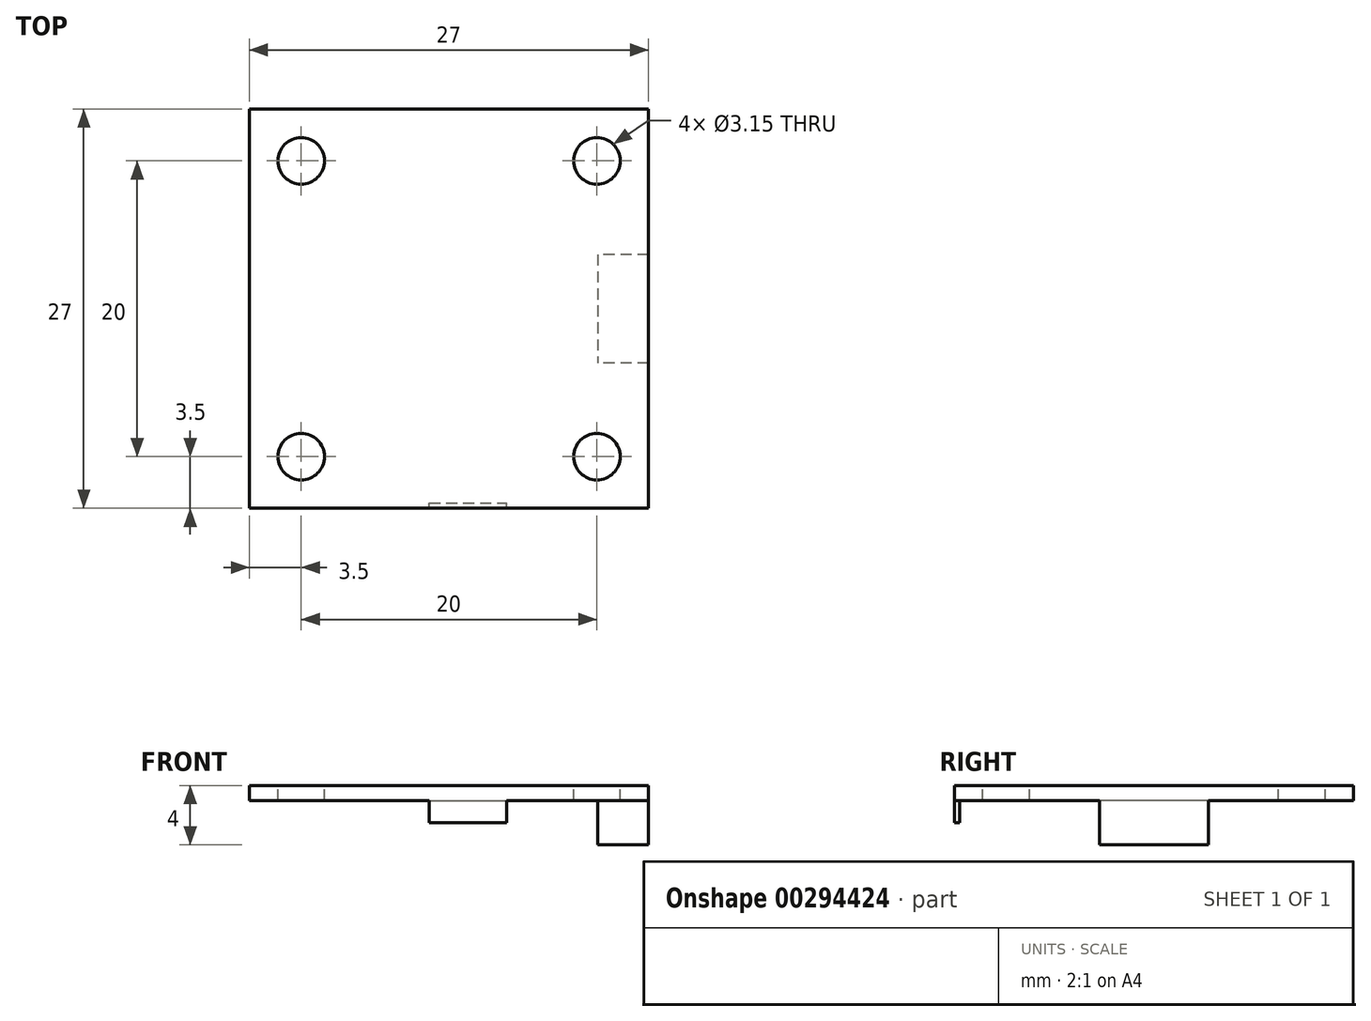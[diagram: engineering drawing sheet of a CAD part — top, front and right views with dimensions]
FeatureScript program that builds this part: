
annotation { "Feature Type Name" : "Feature", "Feature Type Description" : "" }
export const myFeature = defineFeature(function(context is Context, id is Id, definition is map)
    precondition{}
    {
        {
            var Q0;
            Q0=qCreatedBy(makeId("Top.planeOp"),FACE);
            var sketch = newSketch(context, id + "F0", { "sketchPlane" : qUnion([Q0])});
            skLineSegment(sketch, "E0.bottom", {"start": v(-13.5, 13.5) * mm, "end": v(13.5, 13.5) * mm});
            skLineSegment(sketch, "E0.top", {"start": v(-13.5, -13.5) * mm, "end": v(13.5, -13.5) * mm});
            skLineSegment(sketch, "E0.left", {"start": v(-13.5, 13.5) * mm, "end": v(-13.5, -13.5) * mm});
            skLineSegment(sketch, "E0.right", {"start": v(13.5, 13.5) * mm, "end": v(13.5, -13.5) * mm});
            skPoint(sketch, "E0.middle", {"position": v(0, 0) * mm});
            skLineSegment(sketch, "E1.bottom", {"start": v(-10, 10) * mm, "end": v(10, 10) * mm, "construction": true});
            skLineSegment(sketch, "E1.top", {"start": v(-10, -10) * mm, "end": v(10, -10) * mm, "construction": true});
            skLineSegment(sketch, "E1.left", {"start": v(-10, 10) * mm, "end": v(-10, -10) * mm, "construction": true});
            skLineSegment(sketch, "E1.right", {"start": v(10, 10) * mm, "end": v(10, -10) * mm, "construction": true});
            skSolve(sketch);
        }
        {
            var Q0;
            Q0 = qSketchRegion(id + "F0", true);
            extrude(context, id + "F1", {"entities" : qUnion([Q0]), "oppositeDirection" : true, "depth" : 1 * mm});
        }
        {
            var Q0;
            Q0=sQuery(id+"F0.wireOp",VERTEX,"E1.right.start");
            var Q1;
            Q1=sQuery(id+"F0.wireOp",VERTEX,"E1.right.end");
            var Q2;
            Q2=sQuery(id+"F0.wireOp",VERTEX,"E1.left.end");
            var Q3;
            Q3=sQuery(id+"F0.wireOp",VERTEX,"E1.left.start");
            var Q4;
            Q4=makeQuery(id+"F1.opExtrude","SWEPT_BODY",BODY,{"disambiguationData":[OSD([sQuery(id+"F0.wireOp",EDGE,"E0.bottom"),sQuery(id+"F0.wireOp",EDGE,"E0.top"),sQuery(id+"F0.wireOp",EDGE,"E0.left"),sQuery(id+"F0.wireOp",EDGE,"E0.right")])]});
            hole(context, id + "F2", {"style" : HoleStyle.SIMPLE, "endStyle" : HoleEndStyle.THROUGH, "standardTappedOrClearance" : lookupTablePath({ "standard" : "ISO", "fit" : "Close", "size" : "M3", "type" : "Clearance" }), "standardBlindInLast" : lookupTablePath({ "fit" : "Close", "standard" : "ISO", "size" : "M3", "type" : "Clearance" }), "holeDiameter" : 3.15 * mm, "tappedDepth" : 12.7 * mm, "tapClearance" : 3, "locations" : qUnion([Q0, Q1, Q2, Q3]), "scope" : qUnion([Q4])});
        }
        {
            var Q0;
            Q0=makeQuery(id+"F1.opExtrude","CAP_FACE",FACE,{"disambiguationData":[OSD([sQuery(id+"F0.wireOp",EDGE,"E0.bottom"),sQuery(id+"F0.wireOp",EDGE,"E0.top"),sQuery(id+"F0.wireOp",EDGE,"E0.left"),sQuery(id+"F0.wireOp",EDGE,"E0.right")])],"isStart":false});
            var sketch = newSketch(context, id + "F3", { "sketchPlane" : qUnion([Q0])});
            skLineSegment(sketch, "E2.bottom", {"start": v(13.5, -3.67) * mm, "end": v(10.05, -3.67) * mm});
            skLineSegment(sketch, "E2.top", {"start": v(13.5, 3.67) * mm, "end": v(10.05, 3.67) * mm});
            skLineSegment(sketch, "E2.left", {"start": v(13.5, -3.67) * mm, "end": v(13.5, 3.67) * mm});
            skLineSegment(sketch, "E2.right", {"start": v(10.05, -3.67) * mm, "end": v(10.05, 3.67) * mm});
            skPoint(sketch, "E3", {"position": v(10.05, 0) * mm});
            skSolve(sketch);
        }
        {
            var Q0;
            Q0 = qSketchRegion(id + "F3", true);
            extrude(context, id + "F4", {"entities" : qUnion([Q0]), "operationType" : NewBodyOperationType.ADD, "depth" : 3 * mm});
        }
        {
            var Q0;
            Q0=makeQuery(id+"F0.imprint","IMPRINT",FACE,{"disambiguationData":[TD([[makeQuery(id+"F0.imprint","IMPRINT",EDGE,{"derivedFrom":sQuery(id+"F0.wireOp",EDGE,"E0.bottom")}),-1.0]])]});
            var sketch = newSketch(context, id + "F5", { "sketchPlane" : qUnion([Q0])});
            skLineSegment(sketch, "E4.bottom", {"start": v(-1.34, -18.06) * mm, "end": v(3.9, -18.06) * mm});
            skLineSegment(sketch, "E4.top", {"start": v(-1.34, -13.15) * mm, "end": v(3.9, -13.15) * mm});
            skLineSegment(sketch, "E4.left", {"start": v(-1.34, -18.06) * mm, "end": v(-1.34, -13.15) * mm});
            skLineSegment(sketch, "E4.right", {"start": v(3.9, -18.06) * mm, "end": v(3.9, -13.15) * mm});
            skSolve(sketch);
        }
        {
            var Q0;
            {var subQ0=sQuery(id+"F5.wireOp",EDGE,"E4.top");Q0=makeQuery(id+"F5.imprint","IMPRINT",FACE,{"disambiguationData":[TD([[makeQuery(id+"F5.imprint","IMPRINT",EDGE,{"derivedFrom":subQ0}),-1.0]])]});}
            extrude(context, id + "F6", {"entities" : qUnion([Q0]), "operationType" : NewBodyOperationType.ADD, "oppositeDirection" : true, "depth" : 2.5 * mm});
        }
    });
